# Revit family: 230654KCG01-011_230654KCG01-011-KMMS130RPS
name_source: partatom
category: Specialty Equipment
units: mm (PartAtom-declared; Revit-internal decimal feet)

## family parameters
Always vertical = Yes
Cut with Voids When Loaded = No
Enable Cutting in Views = No
Maintain Annotation Orientation = No
Part Type = Normal
Room Calculation Point = No
Round Connector Dimension = Use Diameter
Shared = No
Work Plane-Based = No

## types (1)
- KMMS130RPS
    Accent Material = ARCAT - Metal - Steel - Gray - Light
    Apparent Load = 15 VA
    Back Panel = ARCAT - Metal - Steel - Grey(1)
    Black Logo = White Logo
    Body Material = ARCAT - Metal - Steel - Black Stainless
    Clearance Material = ARCAT - Clearance
    Default Elevation = 0"
    Depth = 15 9/16"
    Description = KITCHENAID 1.9 CU. FT CAPACITY MICROWAVE
    Dimension Guide = ETA end of August
    Display Panel Material = ARCAT - Glass - Black
    Display Side = ARCAT - Metal - Steel - Black(1)
    Display Unit = ARCAT - Metal - Steel - Black Stainless
    Door Frame = ARCAT - Metal - Steel - Grey
    Door Front Glass Material = ARCAT - Glass - Black
    Door Material = ARCAT - Metal - Steel - Gray - Light
    Family Name = KA Titan
    Feature 1 = Auto Functions
    Feature 2 = 1.9 Cu. Ft. Capacity
    Feature 3 = 3-Speed 400 CFM Motor Class* Ventilation System

*Peak Performance varies based on installation.  Resources available at AHAM.org
3-Speed 400 CFM Motor Class* Ventilation System

*Peak Performance varies based on installation.  Resources available at AHAM.org
    Glass Material = ARCAT - Glass - Tempered - Black
    Height = 17 1/8"
    Hz = 60 CF
    Installation-Fabrication = https://www.whirlpool.com
    Style Master = ARCAT - Metal - Steel - Stainless - Light(1)
    Voltage = 120 V
    Width = 29 7/8"

## geometry (parser evidence)
native form markers: Sweep x9
no freeform markers — native parametric forms only
